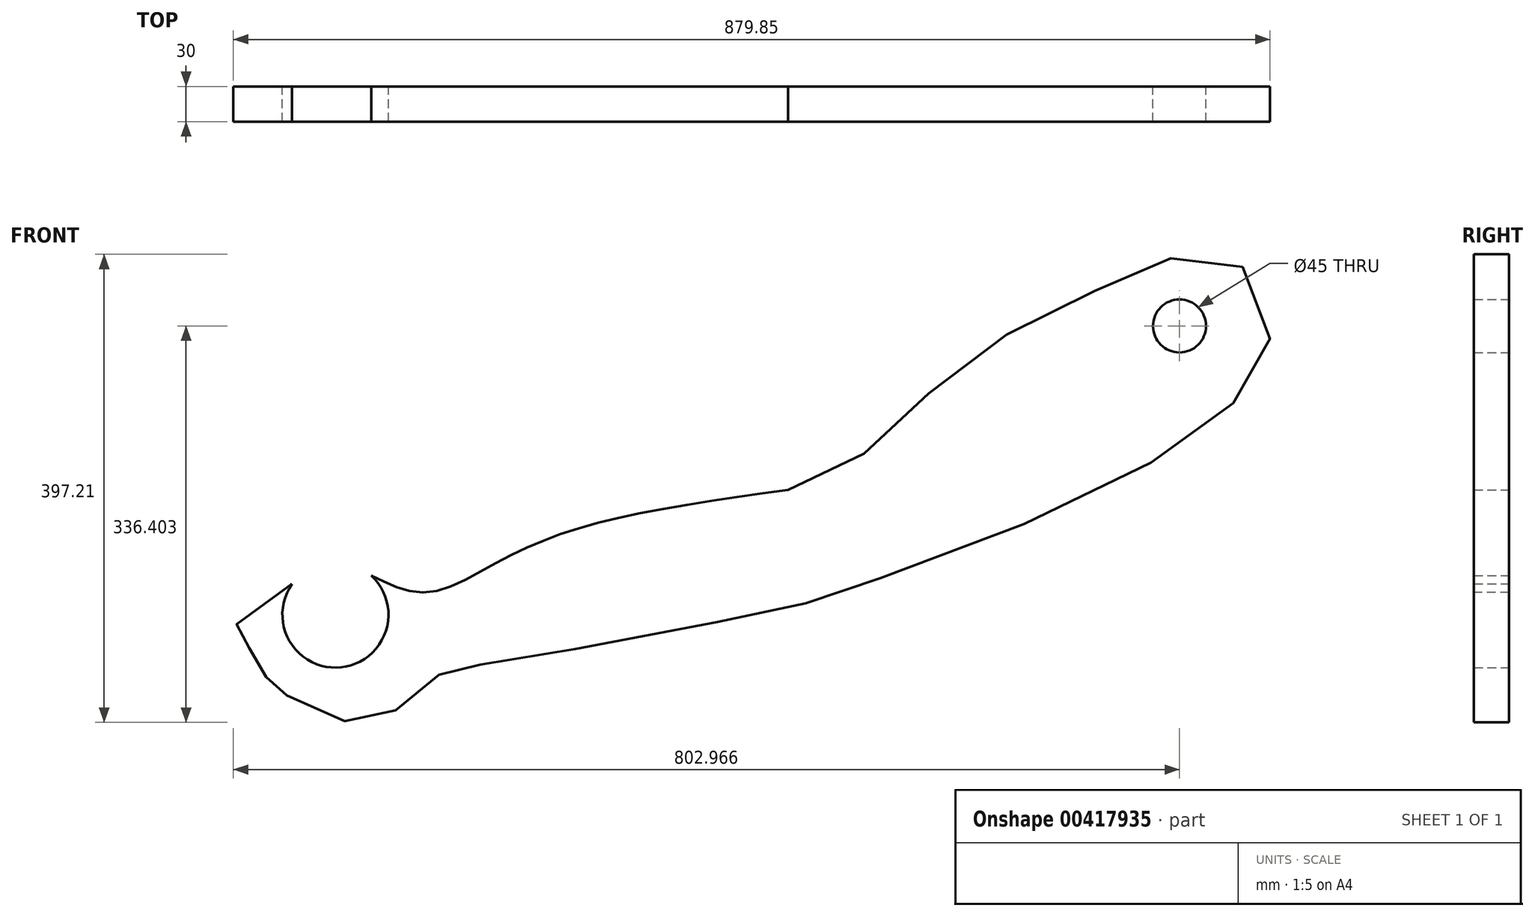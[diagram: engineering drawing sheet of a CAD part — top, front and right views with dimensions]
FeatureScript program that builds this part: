
annotation { "Feature Type Name" : "Feature", "Feature Type Description" : "" }
export const myFeature = defineFeature(function(context is Context, id is Id, definition is map)
    precondition{}
    {
        {
            var Q0;
            Q0=qCreatedBy(makeId("Front.planeOp"),FACE);
            var sketch = newSketch(context, id + "F0", { "sketchPlane" : qUnion([Q0])});
            skFitSpline(sketch, "E0", {"points": [v(4.8, -0.26) * mm, v(9.74, 2.26) * mm, v(14.47, 6.78) * mm, v(21.3, 10.56) * mm, v(26.4, 12.81) * mm, v(30.49, 12.35) * mm, v(32.03, 8.06) * mm, v(29.61, 4.3) * mm, v(20.4, -1.23) * mm, v(6.7, -6.39) * mm, v(5.12, -6.85) * mm, v(-7.46, -9.3) * mm, v(-13.35, -10.24) * mm, v(-14.41, -10.43) * mm, v(-16.12, -11.67) * mm, v(-18, -13.1) * mm, v(-20.18, -13.36) * mm, v(-23.48, -12.06) * mm, v(-23.77, -11.45) * mm, v(-24.62, -11.2) * mm, v(-24.84, -10.41) * mm, v(-25.63, -9.67) * mm, v(-25.76, -8.94) * mm, v(-26.55, -8.32) * mm, v(-26.35, -7.8) * mm, v(-23.26, -5.59) * mm], "startDerivative": vector(102.24, 40.24) * mm, "endDerivative": vector(86.36, 54.01) * mm});
            skCircle(sketch, "E1", {"center": v(-20.82, -7.32) * mm, "radius": 3 * mm});
            skCircle(sketch, "E2", {"center": v(26.94, 9) * mm, "radius": 1.5 * mm});
            skFitSpline(sketch, "E3", {"points": [v(-18.8, -5.1) * mm, v(-15.64, -6.06) * mm, v(-11.4, -4.23) * mm, v(-5.67, -2.06) * mm, v(4.8, -0.26) * mm], "startDerivative": vector(16.4, -8.32) * mm, "endDerivative": vector(33.56, 4.68) * mm});
            skSolve(sketch);
        }
        {
            var Q0;
            {var subQ0=sQuery(id+"F0.wireOp",EDGE,"E0");Q0=makeQuery(id+"F0.imprint","IMPRINT",FACE,{"disambiguationData":[TD([[makeQuery(id+"F0.imprint","IMPRINT",EDGE,{"derivedFrom":subQ0}),-1.0]])]});}
            extrude(context, id + "F1", {"entities" : qUnion([Q0]), "depth" : 2 * mm, "offsetDistance" : 25 * mm});
        }
        {
            var Q0;
            Q0=makeQuery(id+"F1.opExtrude","SWEPT_BODY",BODY,{"disambiguationData":[OSD([sQuery(id+"F0.wireOp",EDGE,"E0"),sQuery(id+"F0.wireOp",EDGE,"E1"),sQuery(id+"F0.wireOp",EDGE,"E2"),sQuery(id+"F0.wireOp",EDGE,"E3")])]});
            var Q1;
            Q1=sQuery(id+"F0.wireOp",VERTEX,"E0.end");
            transform(context, id + "F2", {"entities" : qUnion([Q0]), "transformType" : TransformType.SCALE_UNIFORMLY, "scale" : 10, "scalePoint" : qUnion([Q1]), "makeCopy" : false});
        }
        {
            var Q0;
            Q0=makeQuery(id+"F1.opExtrude","SWEPT_BODY",BODY,{"disambiguationData":[OSD([sQuery(id+"F0.wireOp",EDGE,"E0"),sQuery(id+"F0.wireOp",EDGE,"E1"),sQuery(id+"F0.wireOp",EDGE,"E2"),sQuery(id+"F0.wireOp",EDGE,"E3")])]});
            var Q1;
            Q1=qCreatedBy(makeId("Origin.pointOp"),VERTEX);
            transform(context, id + "F3", {"entities" : qUnion([Q0]), "transformType" : TransformType.SCALE_UNIFORMLY, "scale" : 1.5, "scalePoint" : qUnion([Q1]), "makeCopy" : false});
        }
    });
